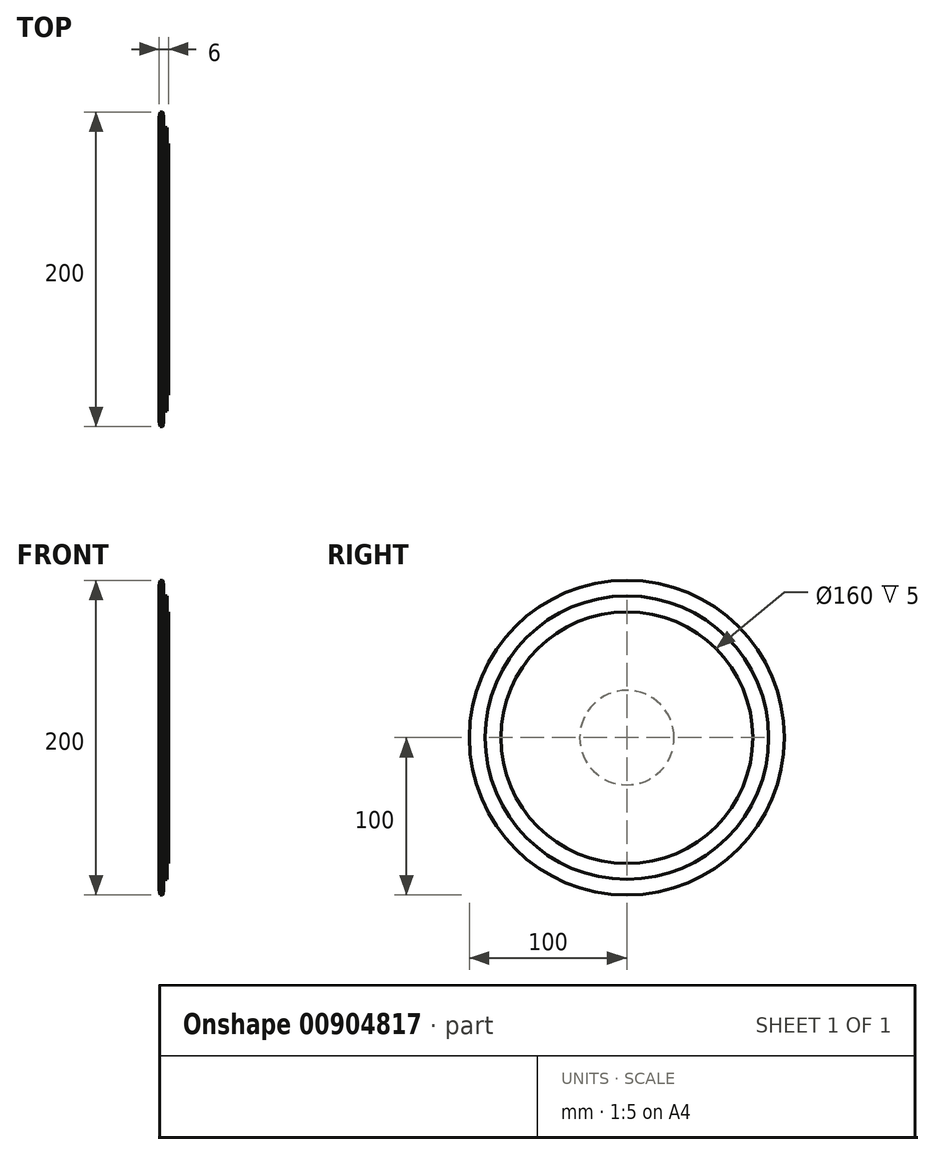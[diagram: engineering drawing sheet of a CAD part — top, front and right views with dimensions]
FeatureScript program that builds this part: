
annotation { "Feature Type Name" : "Feature", "Feature Type Description" : "" }
export const myFeature = defineFeature(function(context is Context, id is Id, definition is map)
    precondition{}
    {
        {
            var Q0;
            Q0=qCreatedBy(makeId("Front.planeOp"),FACE);
            var sketch = newSketch(context, id + "F0", { "sketchPlane" : qUnion([Q0])});
            skLineSegment(sketch, "E0", {"start": v(0, 0) * mm, "end": v(5, 0) * mm});
            skLineSegment(sketch, "E1", {"start": v(5, 0) * mm, "end": v(5, -90) * mm});
            skLineSegment(sketch, "E2", {"start": v(5, -90) * mm, "end": v(3, -90) * mm});
            skLineSegment(sketch, "E3", {"start": v(3, -90) * mm, "end": v(3, -95) * mm});
            skLineSegment(sketch, "E4", {"start": v(3, -95) * mm, "end": v(0, -95) * mm});
            skLineSegment(sketch, "E5", {"start": v(0, -95) * mm, "end": v(0, 0) * mm});
            skPoint(sketch, "E6.startSnap0", {"position": v(1.5, -95) * mm});
            skArc(sketch, "E7", {"start": v(0, -95) * mm, "mid": v(0.19, -97.53) * mm, "end": v(0.75, -100) * mm});
            skArc(sketch, "E8", {"start": v(2.25, -100) * mm, "mid": v(2.81, -97.53) * mm, "end": v(3, -95) * mm});
            skPoint(sketch, "E9.orphan", {"position": v(0, -100) * mm});
            skLineSegment(sketch, "E10", {"start": v(0.75, -100) * mm, "end": v(2.25, -100) * mm});
            skSolve(sketch);
        }
        {
            var Q0;
            Q0=makeQuery(id+"F0.imprint","IMPRINT",FACE,{"disambiguationData":[TD([[makeQuery(id+"F0.imprint","IMPRINT",EDGE,{"derivedFrom":sQuery(id+"F0.wireOp",EDGE,"E0")}),-1.0]])]});
            var Q1;
            Q1=makeQuery(id+"F0.imprint","IMPRINT",FACE,{"disambiguationData":[TD([[makeQuery(id+"F0.imprint","IMPRINT",EDGE,{"derivedFrom":sQuery(id+"F0.wireOp",EDGE,"E4")}),1.0]])]});
            var Q2;
            Q2=sQuery(id+"F0.wireOp",EDGE,"E0");
            revolve(context, id + "F1", {"surfaceOperationType" : NewSurfaceOperationType.NEW, "entities" : qUnion([Q0, Q1]), "axis" : qUnion([Q2]), "revolveType" : RevolveType.FULL});
        }
        {
            var Q0;
            Q0=makeQuery(id+"F1.opRevolve","SWEPT_FACE",FACE,{"disambiguationData":[OSD([sQuery(id+"F0.wireOp",EDGE,"E1")])]});
            var sketch = newSketch(context, id + "F2", { "sketchPlane" : qUnion([Q0])});
            skCircle(sketch, "E11", {"center": v(0, 0) * mm, "radius": 20 * mm});
            skCircle(sketch, "E12", {"center": v(0, 0) * mm, "radius": 80 * mm});
            skCircle(sketch, "E13", {"center": v(0, 0) * mm, "radius": 30 * mm});
            skSolve(sketch);
        }
        {
            var Q0;
            Q0 = qSketchRegion(id + "F2", true);
            extrude(context, id + "F3", {"entities" : qUnion([Q0]), "operationType" : NewBodyOperationType.REMOVE, "endBound" : BoundingType.THROUGH_ALL, "oppositeDirection" : true, "depth" : 25.4 * mm, "offsetDistance" : 25.4 * mm});
        }
        {
            var Q0;
            Q0 = qSketchRegion(id + "F2", true);
            var Q1;
            Q1=makeQuery(id+"F3.boolean.opBoolean","SPLIT",FACE,{"disambiguationData":[TD([makeQuery(id+"F3.opExtrude","SWEPT_FACE",FACE,{"disambiguationData":[OSD([sQuery(id+"F2.wireOp",EDGE,"E13")])]})])],"derivedFrom":makeQuery(id+"F1.opRevolve","SWEPT_FACE",FACE,{"disambiguationData":[OSD([sQuery(id+"F0.wireOp",EDGE,"E1")])]})});
            extrude(context, id + "F4", {"entities" : qUnion([Q0, Q1]), "operationType" : NewBodyOperationType.ADD, "depth" : 1 * mm, "offsetDistance" : 25.4 * mm});
        }
    });
